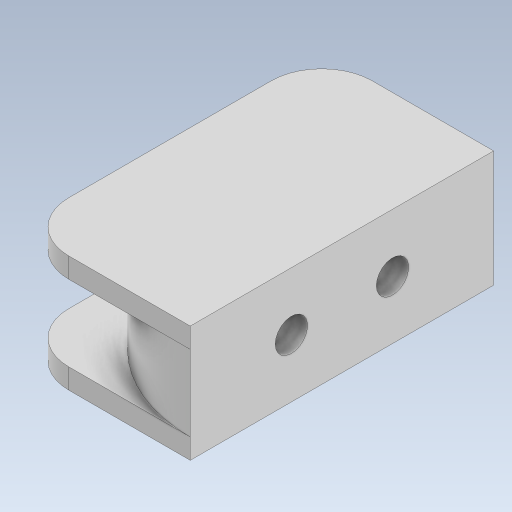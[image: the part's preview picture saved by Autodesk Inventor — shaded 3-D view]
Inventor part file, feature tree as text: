
AUTODESK INVENTOR PART (.ipt)
format: ipt  version: 2023.5 (Build 275446000, 446)  size: 342,528 bytes
history: native  units: mm
features: extrude x5, sketch x4, plane x1, fillet x1
ambient origin geometry x8: Origin, YZ Plane, XZ Plane, XY Plane, X Axis, Y Axis, Z Axis, Center Point
bodies: Body1 (feature_tree)
feature tree (11):
  extrude  "Extrusion2"  Depth=11.5mm TaperAngle=0.0deg
  extrude  "Extrusion3"  Depth=2.0mm TaperAngle=0.0deg
  extrude  "Extrusion4"  Depth=10.0mm
  plane  "Work Plane1"
  sketch  "Sketch5"  dims[d12=3.2mm d13=10.0mm d14=5.5mm d15=5.5mm d16=15.0mm d17=0.0mm d18=9.0mm d19=0.0mm d20=5.0mm]
  extrude  "Extrusion5"  Depth=10.0mm
  extrude  "Extrusion6"  Depth=5.0mm
  fillet  "Fillet1"  Radius=5.5mm
  sketch  "Sketch1"  dims[d0=30.0mm d3=11.5mm d4=0.0mm]
  sketch  "Sketch2"  dims[d5=2.0mm d6=0.0mm d7=2.0mm d8=0.0mm]
  sketch  "Sketch3"  dims[d10=3.2mm d11=10.0mm]
